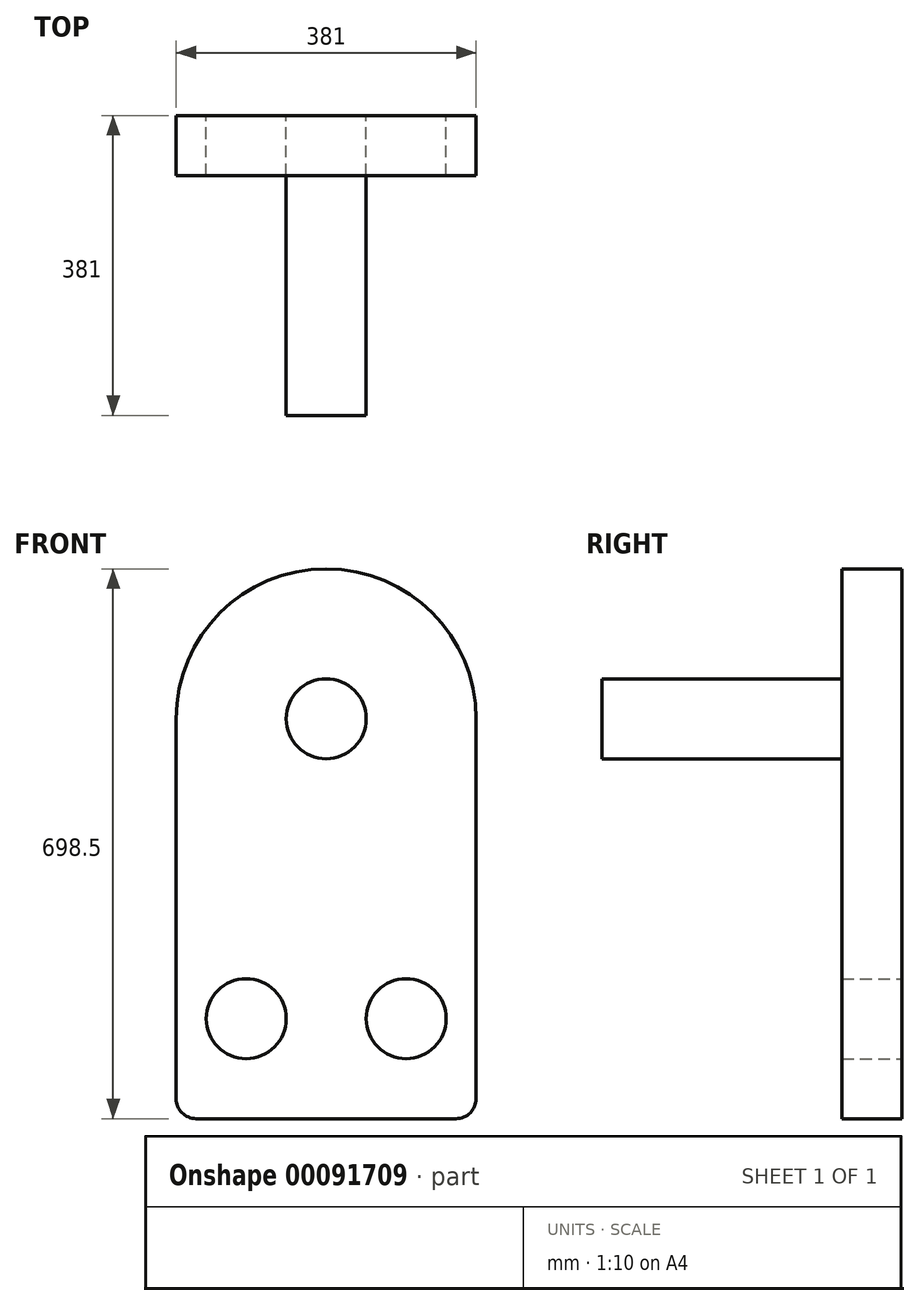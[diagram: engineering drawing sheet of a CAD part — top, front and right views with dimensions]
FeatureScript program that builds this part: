
annotation { "Feature Type Name" : "Feature", "Feature Type Description" : "" }
export const myFeature = defineFeature(function(context is Context, id is Id, definition is map)
    precondition{}
    {
        {
            var Q0;
            Q0=qCreatedBy(makeId("Front.planeOp"),FACE);
            var sketch = newSketch(context, id + "F0", { "sketchPlane" : qUnion([Q0])});
            skLineSegment(sketch, "E0.bottom", {"start": v(0, 0) * mm, "end": v(-381, 0) * mm});
            skLineSegment(sketch, "E0.left", {"start": v(0, 0) * mm, "end": v(0, 508) * mm});
            skLineSegment(sketch, "E0.right", {"start": v(-381, 0) * mm, "end": v(-381, 508) * mm});
            skArc(sketch, "E1", {"start": v(0, 508) * mm, "mid": v(-190.5, 698.5) * mm, "end": v(-381, 508) * mm});
            skCircle(sketch, "E2", {"center": v(-190.5, 508) * mm, "radius": 50.8 * mm});
            skCircle(sketch, "E3", {"center": v(-292.1, 127) * mm, "radius": 50.8 * mm});
            skCircle(sketch, "E4", {"center": v(-88.9, 127) * mm, "radius": 50.8 * mm});
            skLineSegment(sketch, "E5", {"start": v(-190.5, 508) * mm, "end": v(-190.5, 105.14) * mm, "construction": true});
            skLineSegment(sketch, "E6", {"start": v(-292.1, 127) * mm, "end": v(-88.9, 127) * mm, "construction": true});
            skSolve(sketch);
        }
        {
            var Q0;
            Q0 = qSketchRegion(id + "F0", true);
            extrude(context, id + "F1", {"entities" : qUnion([Q0]), "depth" : 76.2 * mm});
        }
        {
            var Q0;
            Q0=makeQuery(id+"F0.imprint","IMPRINT",FACE,{"disambiguationData":[TD([[makeQuery(id+"F0.imprint","IMPRINT",EDGE,{"derivedFrom":sQuery(id+"F0.wireOp",EDGE,"E2")}),1.0]])]});
            extrude(context, id + "F2", {"entities" : qUnion([Q0]), "operationType" : NewBodyOperationType.ADD, "depth" : 381 * mm});
        }
        {
            var Q0;
            Q0=makeQuery(id+"F1.opExtrude","SWEPT_EDGE",EDGE,{"disambiguationData":[OSD([sQuery(id+"F0.wireOp",EDGE,"E0.bottom"),sQuery(id+"F0.wireOp",EDGE,"E0.right")])]});
            var Q1;
            Q1=makeQuery(id+"F1.opExtrude","SWEPT_EDGE",EDGE,{"disambiguationData":[OSD([sQuery(id+"F0.wireOp",EDGE,"E0.bottom"),sQuery(id+"F0.wireOp",EDGE,"E0.left")])]});
            fillet(context, id + "F3", {"entities" : qUnion([Q0, Q1]), "radius" : 25.4 * mm, "tangentPropagation" : true, "allowEdgeOverflow" : false});
        }
    });
